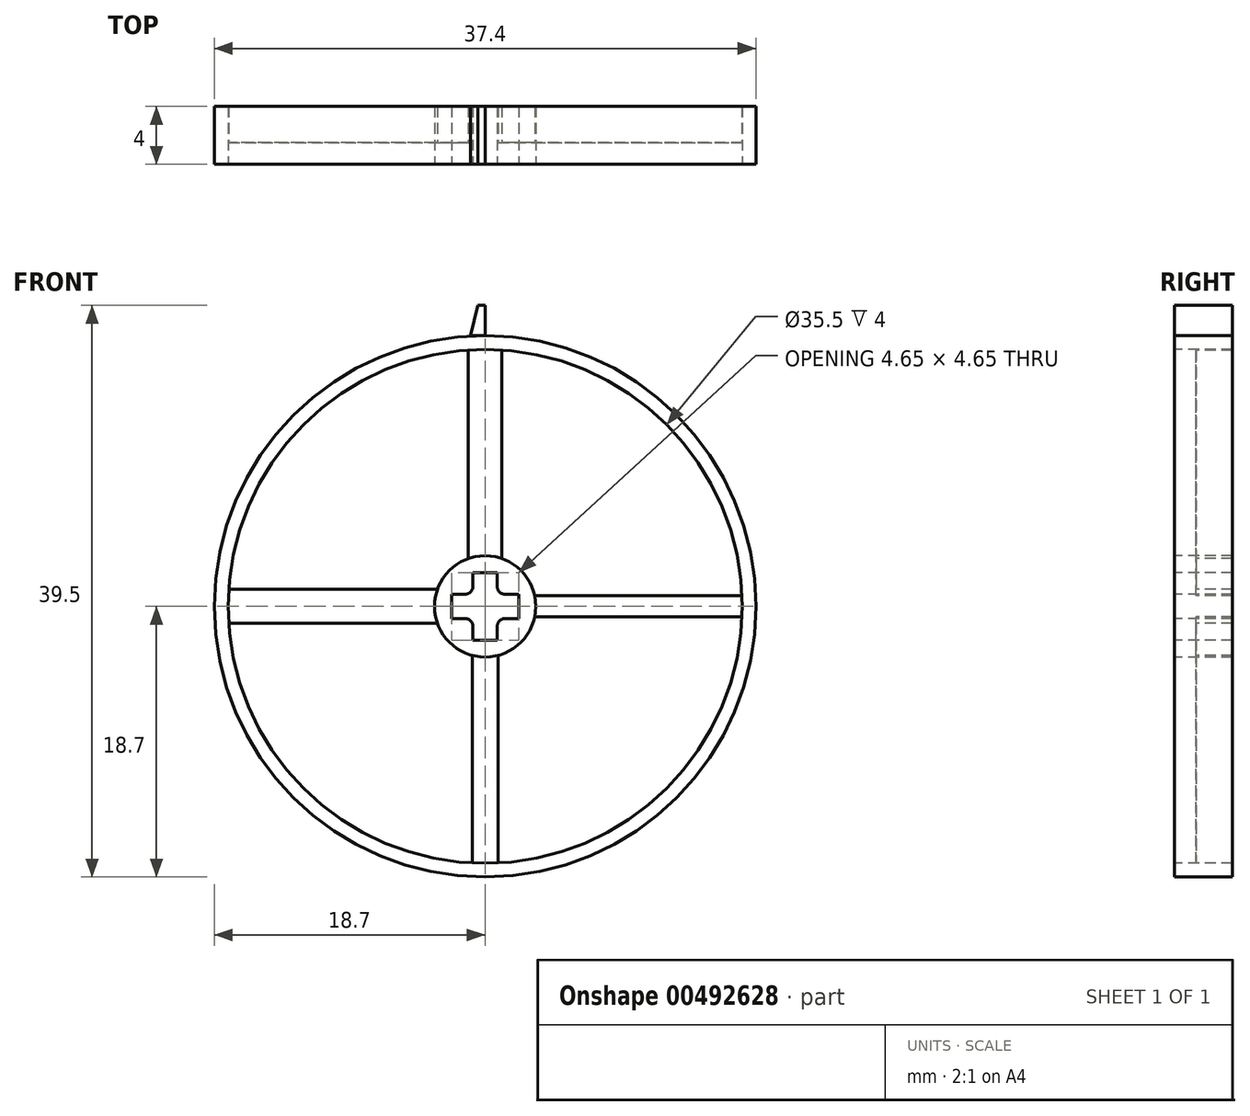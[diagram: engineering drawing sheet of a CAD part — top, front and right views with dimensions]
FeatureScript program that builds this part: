
annotation { "Feature Type Name" : "Feature", "Feature Type Description" : "" }
export const myFeature = defineFeature(function(context is Context, id is Id, definition is map)
    precondition{}
    {
        {
            var Q0;
            Q0=qCreatedBy(makeId("Front.planeOp"),FACE);
            var sketch = newSketch(context, id + "F0", { "sketchPlane" : qUnion([Q0])});
            skCircle(sketch, "E0", {"center": v(0, 0) * mm, "radius": 18.7 * mm});
            skCircle(sketch, "E1", {"center": v(0, 0) * mm, "radius": 20.8 * mm, "construction": true});
            skLineSegment(sketch, "E2", {"start": v(0, 18.7) * mm, "end": v(1, 18.7) * mm});
            skLineSegment(sketch, "E3", {"start": v(1, 18.7) * mm, "end": v(0, 18.7) * mm});
            skLineSegment(sketch, "E4", {"start": v(0, 18.7) * mm, "end": v(-1, 18.7) * mm});
            skLineSegment(sketch, "E5", {"start": v(0, 18.7) * mm, "end": v(0, 20.8) * mm});
            skLineSegment(sketch, "E6", {"start": v(0, 20.8) * mm, "end": v(0.5, 20.8) * mm});
            skLineSegment(sketch, "E7", {"start": v(0, 20.8) * mm, "end": v(-0.5, 20.8) * mm});
            skLineSegment(sketch, "E8", {"start": v(-0.5, 20.8) * mm, "end": v(-1, 18.7) * mm});
            skLineSegment(sketch, "E9", {"start": v(0.5, 20.8) * mm, "end": v(1, 18.7) * mm});
            skLineSegment(sketch, "E10", {"start": v(1, 18.7) * mm, "end": v(1, 18.67) * mm});
            skLineSegment(sketch, "E11", {"start": v(-1, 18.7) * mm, "end": v(-1, 18.67) * mm});
            skSolve(sketch);
        }
        {
            var Q0;
            Q0=makeQuery(id+"F0.imprint","IMPRINT",FACE,{"disambiguationData":[TD([[makeQuery(id+"F0.imprint","IMPRINT",EDGE,{"derivedFrom":sQuery(id+"F0.wireOp",EDGE,"E0")}),1.0]])]});
            extrude(context, id + "F1", {"entities" : qUnion([Q0]), "depth" : 4 * mm, "offsetDistance" : 25 * mm});
        }
        {
            var Q0;
            Q0=makeQuery(id+"F0.imprint","IMPRINT",FACE,{"disambiguationData":[TD([[makeQuery(id+"F0.imprint","IMPRINT",EDGE,{"derivedFrom":sQuery(id+"F0.wireOp",EDGE,"E4")}),-1.0]])]});
            var Q1;
            Q1=makeQuery(id+"F0.imprint","IMPRINT",FACE,{"disambiguationData":[TD([[makeQuery(id+"F0.imprint","IMPRINT",EDGE,{"derivedFrom":sQuery(id+"F0.wireOp",EDGE,"E3")}),-1.0]])]});
            extrude(context, id + "F2", {"entities" : qUnion([Q0, Q1]), "operationType" : NewBodyOperationType.ADD, "depth" : 4 * mm, "offsetDistance" : 25 * mm});
        }
        {
            var Q0;
            Q0=makeQuery(id+"F1.opExtrude","CAP_FACE",FACE,{"disambiguationData":[OSD([sQuery(id+"F0.wireOp",EDGE,"E0")])],"isStart":false});
            var sketch = newSketch(context, id + "F3", { "sketchPlane" : qUnion([Q0])});
            skLineSegment(sketch, "E12", {"start": v(-2.33, 0.85) * mm, "end": v(2.32, 0.85) * mm});
            skLineSegment(sketch, "E13", {"start": v(-2.32, -0.84) * mm, "end": v(2.33, -0.84) * mm});
            skLineSegment(sketch, "E14", {"start": v(0.84, 2.32) * mm, "end": v(0.84, -2.33) * mm});
            skLineSegment(sketch, "E15", {"start": v(-0.85, 2.33) * mm, "end": v(-0.85, -2.32) * mm});
            skLineSegment(sketch, "E16", {"start": v(-2.33, 0.85) * mm, "end": v(-2.32, -0.84) * mm});
            skLineSegment(sketch, "E17", {"start": v(-0.85, 2.33) * mm, "end": v(0.84, 2.32) * mm});
            skLineSegment(sketch, "E18", {"start": v(2.32, 0.85) * mm, "end": v(2.33, -0.84) * mm});
            skLineSegment(sketch, "E19", {"start": v(0.84, -2.33) * mm, "end": v(-0.85, -2.32) * mm});
            skSolve(sketch);
        }
        {
            var Q0;
            Q0 = qSketchRegion(id + "F3", true);
            extrude(context, id + "F4", {"entities" : qUnion([Q0]), "operationType" : NewBodyOperationType.REMOVE, "oppositeDirection" : true, "depth" : 25 * mm, "offsetDistance" : 25 * mm});
        }
        {
            var Q0;
            Q0=makeQuery(id+"F1.opExtrude","CAP_FACE",FACE,{"disambiguationData":[OSD([sQuery(id+"F0.wireOp",EDGE,"E0")])],"isStart":false});
            var sketch = newSketch(context, id + "F5", { "sketchPlane" : qUnion([Q0])});
            skCircle(sketch, "E20", {"center": v(0, 0) * mm, "radius": 17.75 * mm});
            skCircle(sketch, "E21", {"center": v(0, 0) * mm, "radius": 3.5 * mm});
            skSolve(sketch);
        }
        {
            var Q0;
            Q0=makeQuery(id+"F5.imprint","IMPRINT",FACE,{"disambiguationData":[TD([[makeQuery(id+"F5.imprint","IMPRINT",EDGE,{"derivedFrom":sQuery(id+"F5.wireOp",EDGE,"E20")}),1.0]])]});
            extrude(context, id + "F6", {"entities" : qUnion([Q0]), "operationType" : NewBodyOperationType.REMOVE, "oppositeDirection" : true, "depth" : 0.75 * mm, "offsetDistance" : 25 * mm});
        }
        {
            var Q0;
            Q0=makeQuery(id+"F6.boolean.opBoolean","COPY",FACE,{"derivedFrom":makeQuery(id+"F6.opExtrude","CAP_FACE",FACE,{"disambiguationData":[OSD([sQuery(id+"F5.wireOp",EDGE,"E20"),sQuery(id+"F5.wireOp",EDGE,"E21")])],"isStart":false})});
            var sketch = newSketch(context, id + "F7", { "sketchPlane" : qUnion([Q0])});
            skCircle(sketch, "E22", {"center": v(0, 0) * mm, "radius": 17.75 * mm});
            skCircle(sketch, "E23", {"center": v(0, 0) * mm, "radius": 3.5 * mm});
            skSolve(sketch);
        }
        {
            var Q0;
            Q0 = qSketchRegion(id + "F7", true);
            extrude(context, id + "F8", {"entities" : qUnion([Q0]), "operationType" : NewBodyOperationType.REMOVE, "oppositeDirection" : true, "depth" : 0.75 * mm, "offsetDistance" : 25 * mm});
        }
        {
            var Q0;
            Q0=makeQuery(id+"F4.boolean.opBoolean","COPY",EDGE,{"derivedFrom":makeQuery(id+"F4.opExtrude","SWEPT_EDGE",EDGE,{"disambiguationData":[OSD([sQuery(id+"F3.wireOp",EDGE,"E12"),sQuery(id+"F3.wireOp",EDGE,"E15")])]})});
            var Q1;
            Q1=makeQuery(id+"F4.boolean.opBoolean","COPY",EDGE,{"derivedFrom":makeQuery(id+"F4.opExtrude","SWEPT_EDGE",EDGE,{"disambiguationData":[OSD([sQuery(id+"F3.wireOp",EDGE,"E12"),sQuery(id+"F3.wireOp",EDGE,"E14")])]})});
            var Q2;
            Q2=makeQuery(id+"F4.boolean.opBoolean","COPY",EDGE,{"derivedFrom":makeQuery(id+"F4.opExtrude","SWEPT_EDGE",EDGE,{"disambiguationData":[OSD([sQuery(id+"F3.wireOp",EDGE,"E13"),sQuery(id+"F3.wireOp",EDGE,"E15")])]})});
            var Q3;
            Q3=makeQuery(id+"F4.boolean.opBoolean","COPY",EDGE,{"derivedFrom":makeQuery(id+"F4.opExtrude","SWEPT_EDGE",EDGE,{"disambiguationData":[OSD([sQuery(id+"F3.wireOp",EDGE,"E13"),sQuery(id+"F3.wireOp",EDGE,"E14")])]})});
            fillet(context, id + "F9", {"entities" : qUnion([Q0, Q1, Q2, Q3]), "radius" : 0.5 * mm, "tangentPropagation" : true, "allowEdgeOverflow" : false});
        }
        {
            var Q0;
            Q0=makeQuery(id+"F8.boolean.opBoolean","COPY",FACE,{"derivedFrom":makeQuery(id+"F8.opExtrude","CAP_FACE",FACE,{"disambiguationData":[OSD([sQuery(id+"F7.wireOp",EDGE,"E22"),sQuery(id+"F7.wireOp",EDGE,"E23")])],"isStart":false})});
            var sketch = newSketch(context, id + "F10", { "sketchPlane" : qUnion([Q0])});
            skLineSegment(sketch, "E24", {"start": v(1.16, 3.3) * mm, "end": v(1.16, 17.71) * mm});
            skLineSegment(sketch, "E25.MirrorCS", {"start": v(-1.16, 3.3) * mm, "end": v(-1.16, 17.71) * mm});
            skLineSegment(sketch, "E26", {"start": v(3.42, -0.73) * mm, "end": v(17.75, -0.73) * mm});
            skLineSegment(sketch, "E27.MirrorCS", {"start": v(3.42, 0.73) * mm, "end": v(17.75, 0.73) * mm});
            skLineSegment(sketch, "E28", {"start": v(-0.9, -3.38) * mm, "end": v(-0.9, -17.73) * mm});
            skLineSegment(sketch, "E29.MirrorCS", {"start": v(0.9, -3.38) * mm, "end": v(0.9, -17.73) * mm});
            skLineSegment(sketch, "E30", {"start": v(-3.3, -1.18) * mm, "end": v(-17.71, -1.18) * mm});
            skLineSegment(sketch, "E31.MirrorCS", {"start": v(-3.3, 1.18) * mm, "end": v(-17.71, 1.18) * mm});
            skSolve(sketch);
        }
        {
            var Q0;
            {var subQ0=sQuery(id+"F10.wireOp",EDGE,"E30");Q0=makeQuery(id+"F10.imprint","IMPRINT",FACE,{"disambiguationData":[TD([[makeQuery(id+"F10.imprint","IMPRINT",EDGE,{"derivedFrom":subQ0}),-1.0]])]});}
            var Q1;
            {var subQ0=sQuery(id+"F10.wireOp",EDGE,"E28");Q1=makeQuery(id+"F10.imprint","IMPRINT",FACE,{"disambiguationData":[TD([[makeQuery(id+"F10.imprint","IMPRINT",EDGE,{"derivedFrom":subQ0}),1.0]])]});}
            var Q2;
            {var subQ0=sQuery(id+"F10.wireOp",EDGE,"E26");var subQ1=makeQuery(id+"F8.boolean.opBoolean","COPY",EDGE,{"derivedFrom":makeQuery(id+"F8.opExtrude","CAP_EDGE",EDGE,{"disambiguationData":[OSD([sQuery(id+"F7.wireOp",EDGE,"E23")])],"isStart":false})});var subQ2=makeQuery(id+"F10.imprint","INTERSECT",VERTEX,{"derivedFrom":[subQ1,subQ0]});Q2=makeQuery(id+"F10.imprint","IMPRINT",FACE,{"disambiguationData":[TD([[makeQuery(id+"F10.imprint","IMPRINT",EDGE,{"disambiguationData":[TD([[subQ2,-1.0]])],"derivedFrom":subQ0}),1.0]])]});}
            var Q3;
            {var subQ0=sQuery(id+"F10.wireOp",EDGE,"E24");Q3=makeQuery(id+"F10.imprint","IMPRINT",FACE,{"disambiguationData":[TD([[makeQuery(id+"F10.imprint","IMPRINT",EDGE,{"derivedFrom":subQ0}),1.0]])]});}
            extrude(context, id + "F11", {"entities" : qUnion([Q0, Q1, Q2, Q3]), "operationType" : NewBodyOperationType.REMOVE, "oppositeDirection" : true, "depth" : 25 * mm, "offsetDistance" : 25 * mm});
        }
    });
